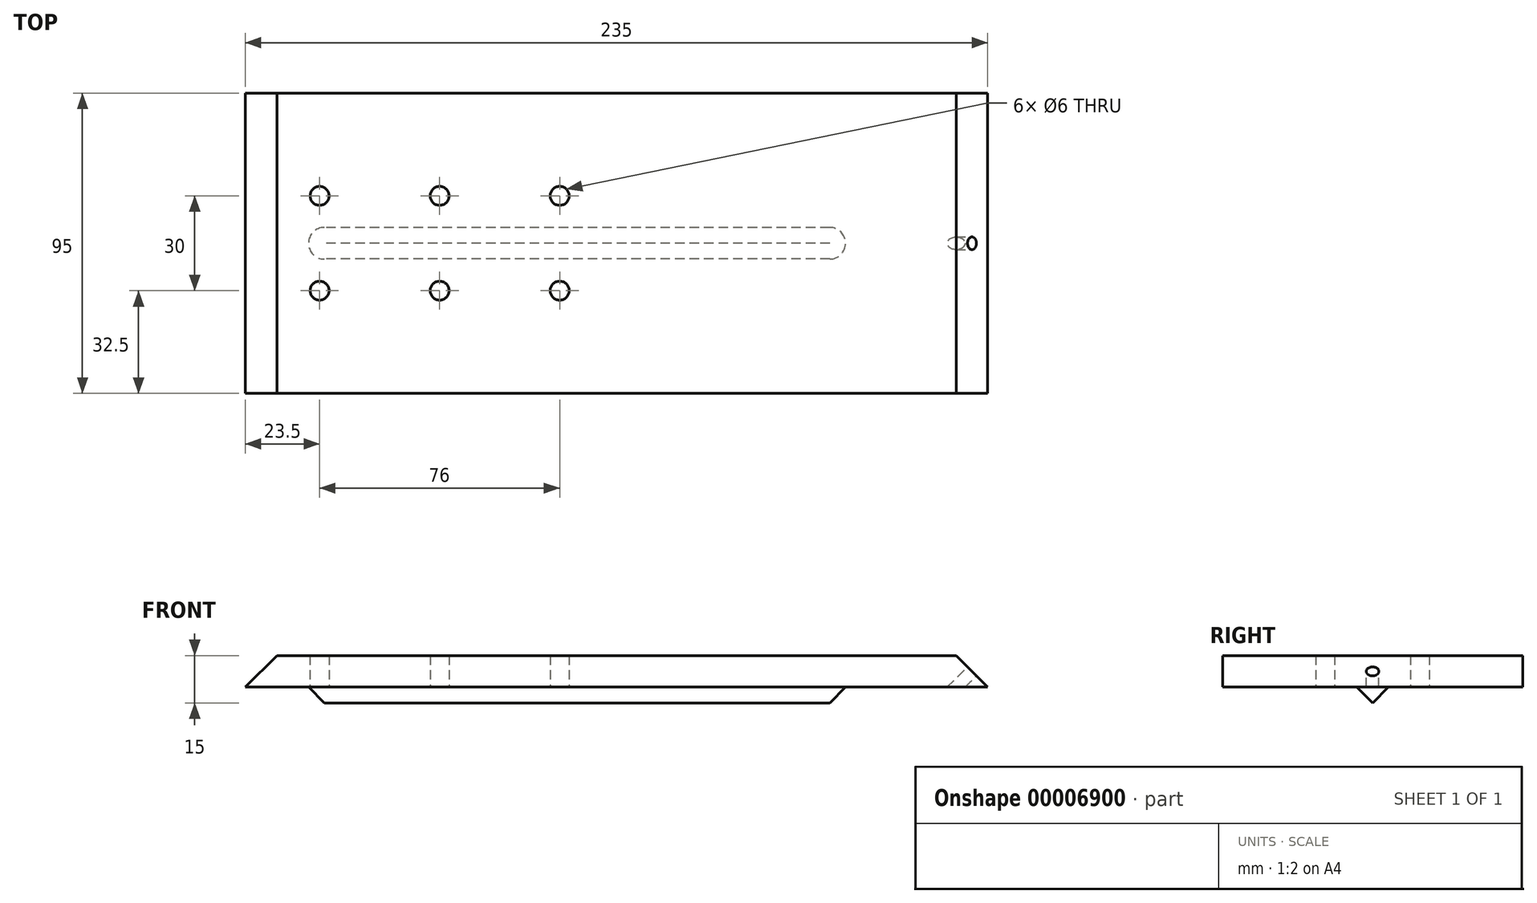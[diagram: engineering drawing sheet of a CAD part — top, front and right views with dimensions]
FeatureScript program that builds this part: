
annotation { "Feature Type Name" : "Feature", "Feature Type Description" : "" }
export const myFeature = defineFeature(function(context is Context, id is Id, definition is map)
    precondition{}
    {
        {
            var Q0;
            Q0=qCreatedBy(makeId("Top.planeOp"),FACE);
            var sketch = newSketch(context, id + "F0", { "sketchPlane" : qUnion([Q0])});
            skLineSegment(sketch, "E0.rect.bottom", {"start": v(125, -47.5) * mm, "end": v(-125, -47.5) * mm});
            skLineSegment(sketch, "E0.rect.top", {"start": v(125, 47.5) * mm, "end": v(-125, 47.5) * mm});
            skLineSegment(sketch, "E0.rect.left", {"start": v(125, -47.5) * mm, "end": v(125, 47.5) * mm});
            skLineSegment(sketch, "E0.rect.right", {"start": v(-125, -47.5) * mm, "end": v(-125, 47.5) * mm});
            skPoint(sketch, "E0.rect.middle", {"position": v(0, 0) * mm});
            skLineSegment(sketch, "E1", {"start": v(-125, 0) * mm, "end": v(125, 0) * mm, "construction": true});
            skLineSegment(sketch, "E2", {"start": v(-101.5, 47.5) * mm, "end": v(-101.5, -47.5) * mm, "construction": true});
            skLineSegment(sketch, "E3", {"start": v(-63.5, 47.5) * mm, "end": v(-63.5, -47.5) * mm, "construction": true});
            skLineSegment(sketch, "E4", {"start": v(-25.5, 47.5) * mm, "end": v(-25.5, -47.5) * mm, "construction": true});
            skCircle(sketch, "E5", {"center": v(-101.5, 15) * mm, "radius": 3 * mm});
            skCircle(sketch, "E6", {"center": v(-63.5, 15) * mm, "radius": 3 * mm});
            skCircle(sketch, "E7", {"center": v(-25.5, 15) * mm, "radius": 3 * mm});
            skCircle(sketch, "E8", {"center": v(-101.5, -15) * mm, "radius": 3 * mm});
            skCircle(sketch, "E9", {"center": v(-63.5, -15) * mm, "radius": 3 * mm});
            skCircle(sketch, "E10", {"center": v(-25.5, -15) * mm, "radius": 3 * mm});
            skSolve(sketch);
        }
        {
            var Q0;
            Q0=qSketchRegion(id+"F0",true);
            var Q1;
            Q1=makeQuery(id+"F0.imprint","IMPRINT",FACE,{"disambiguationData":[TD([[makeQuery(id+"F0.imprint","IMPRINT",EDGE,{"derivedFrom":sQuery(id+"F0.wireOp",EDGE,"E0.rect.bottom")}),-1.0]])]});
            extrude(context, id + "F1", {"entities" : qUnion([Q0, Q1]), "depth" : (15) * mm});
        }
        {
            var Q0;
            Q0=makeQuery(id+"F1.opExtrude","SWEPT_FACE",FACE,{"disambiguationData":[OSD([sQuery(id+"F0.wireOp",EDGE,"E0.rect.right")])]});
            var sketch = newSketch(context, id + "F2", { "sketchPlane" : qUnion([Q0])});
            skLineSegment(sketch, "E11", {"start": v(0, 0) * mm, "end": v(-5, 5) * mm});
            skLineSegment(sketch, "E12", {"start": v(0, 0) * mm, "end": v(5, 5) * mm});
            skLineSegment(sketch, "E13", {"start": v(-5, 5) * mm, "end": v(-47.5, 5) * mm});
            skLineSegment(sketch, "E14", {"start": v(5, 5) * mm, "end": v(47.5, 5) * mm});
            skSolve(sketch);
        }
        {
            var Q0;
            Q0 = qSketchRegion(id + "F2", true);
            var Q1;
            {var subQ2=sQuery(id+"F2.wireOp",EDGE,"E11");Q1=makeQuery(id+"F2.imprint","IMPRINT",FACE,{"disambiguationData":[TD([[makeQuery(id+"F2.imprint","IMPRINT",EDGE,{"derivedFrom":subQ2}),1.0]])]});}
            var Q2;
            {var subQ2=sQuery(id+"F2.wireOp",EDGE,"E12");Q2=makeQuery(id+"F2.imprint","IMPRINT",FACE,{"disambiguationData":[TD([[makeQuery(id+"F2.imprint","IMPRINT",EDGE,{"derivedFrom":subQ2}),-1.0]])]});}
            extrude(context, id + "F3", {"entities" : qUnion([Q0, Q1, Q2]), "operationType" : NewBodyOperationType.REMOVE, "endBound" : BoundingType.THROUGH_ALL, "oppositeDirection" : true, "depth" : 25 * mm});
        }
        {
            var Q0;
            Q0=makeQuery(id+"F1.opExtrude","SWEPT_FACE",FACE,{"disambiguationData":[OSD([sQuery(id+"F0.wireOp",EDGE,"E0.rect.right")])]});
            var sketch = newSketch(context, id + "F4", { "sketchPlane" : qUnion([Q0])});
            skLineSegment(sketch, "E15", {"start": v(-5, 5) * mm, "end": v(5, 5) * mm});
            skSolve(sketch);
        }
        {
            var Q0;
            Q0 = qSketchRegion(id + "F4", true);
            var Q1;
            Q1=makeQuery(id+"F4.imprint","IMPRINT",FACE,{"disambiguationData":[TD([[makeQuery(id+"F4.imprint","IMPRINT",EDGE,{"derivedFrom":sQuery(id+"F4.wireOp",EDGE,"E15")}),-1.0]])]});
            extrude(context, id + "F5", {"entities" : qUnion([Q0, Q1]), "operationType" : NewBodyOperationType.REMOVE, "oppositeDirection" : true, "depth" : 25 * mm});
        }
        {
            var Q0;
            Q0=makeQuery(id+"F5.boolean.opBoolean","COPY",FACE,{"derivedFrom":makeQuery(id+"F5.opExtrude","CAP_FACE",FACE,{"disambiguationData":[OSD([sQuery(id+"F2.wireOp",EDGE,"E11"),sQuery(id+"F2.wireOp",EDGE,"E12"),sQuery(id+"F4.wireOp",EDGE,"E15")])],"isStart":false})});
            var sketch = newSketch(context, id + "F6", { "sketchPlane" : qUnion([Q0])});
            skLineSegment(sketch, "E16", {"start": v(0, 0) * mm, "end": v(0, 5) * mm});
            skSolve(sketch);
        }
        {
            var Q0;
            {var subQ1=sQuery(id+"F6.wireOp",EDGE,"E16");Q0=makeQuery(id+"F6.imprint","IMPRINT",FACE,{"disambiguationData":[TD([[makeQuery(id+"F6.imprint","IMPRINT",EDGE,{"derivedFrom":subQ1}),1.0]])]});}
            var Q1;
            Q1=sQuery(id+"F6.wireOp",EDGE,"E16");
            revolve(context, id + "F7", {"operationType" : NewBodyOperationType.ADD, "entities" : qUnion([Q0]), "axis" : qUnion([Q1]), "revolveType" : RevolveType.FULL});
        }
        {
            var Q0;
            Q0=makeQuery(id+"F1.opExtrude","SWEPT_FACE",FACE,{"disambiguationData":[OSD([sQuery(id+"F0.wireOp",EDGE,"E0.rect.top")])]});
            var sketch = newSketch(context, id + "F8", { "sketchPlane" : qUnion([Q0])});
            skLineSegment(sketch, "E17", {"start": v(125, 5) * mm, "end": v(115, 15) * mm});
            skSolve(sketch);
        }
        {
            var Q0;
            Q0 = qSketchRegion(id + "F8", true);
            var Q1;
            {var subQ2=sQuery(id+"F8.wireOp",EDGE,"E17");Q1=makeQuery(id+"F8.imprint","IMPRINT",FACE,{"disambiguationData":[TD([[makeQuery(id+"F8.imprint","IMPRINT",EDGE,{"derivedFrom":subQ2}),-1.0]])]});}
            extrude(context, id + "F9", {"entities" : qUnion([Q0, Q1]), "operationType" : NewBodyOperationType.REMOVE, "endBound" : BoundingType.THROUGH_ALL, "oppositeDirection" : true, "depth" : 25 * mm});
        }
        {
            var Q0;
            Q0=makeQuery(id+"F1.opExtrude","SWEPT_FACE",FACE,{"disambiguationData":[OSD([sQuery(id+"F0.wireOp",EDGE,"E0.rect.left")])]});
            extrude(context, id + "F10", {"entities" : qUnion([Q0]), "operationType" : NewBodyOperationType.REMOVE, "oppositeDirection" : true, "depth" : (15) * mm});
        }
        {
            var Q0;
            Q0=makeQuery(id+"F10.boolean.opBoolean","COPY",FACE,{"derivedFrom":makeQuery(id+"F10.opExtrude","CAP_FACE",FACE,{"disambiguationData":[OSD([sQuery(id+"F0.wireOp",EDGE,"E0.rect.left")])],"isStart":false})});
            var sketch = newSketch(context, id + "F11", { "sketchPlane" : qUnion([Q0])});
            skLineSegment(sketch, "E18", {"start": v(-5, 5) * mm, "end": v(5, 5) * mm});
            skSolve(sketch);
        }
        {
            var Q0;
            Q0=makeQuery(id+"F11.imprint","IMPRINT",FACE,{"disambiguationData":[TD([[makeQuery(id+"F11.imprint","IMPRINT",EDGE,{"derivedFrom":sQuery(id+"F11.wireOp",EDGE,"E18")}),-1.0]])]});
            extrude(context, id + "F12", {"entities" : qUnion([Q0]), "operationType" : NewBodyOperationType.REMOVE, "oppositeDirection" : true, "depth" : (50) * mm});
        }
        {
            var Q0;
            Q0=makeQuery(id+"F12.boolean.opBoolean","COPY",FACE,{"derivedFrom":makeQuery(id+"F12.opExtrude","CAP_FACE",FACE,{"disambiguationData":[OSD([sQuery(id+"F0.wireOp",EDGE,"E0.rect.left"),sQuery(id+"F2.wireOp",EDGE,"E11"),sQuery(id+"F2.wireOp",EDGE,"E12"),sQuery(id+"F11.wireOp",EDGE,"E18")])],"isStart":false})});
            var sketch = newSketch(context, id + "F13", { "sketchPlane" : qUnion([Q0])});
            skLineSegment(sketch, "E19", {"start": v(0, 0) * mm, "end": v(0, 5) * mm});
            skSolve(sketch);
        }
        {
            var Q0;
            {var subQ1=sQuery(id+"F13.wireOp",EDGE,"E19");Q0=makeQuery(id+"F13.imprint","IMPRINT",FACE,{"disambiguationData":[TD([[makeQuery(id+"F13.imprint","IMPRINT",EDGE,{"derivedFrom":subQ1}),-1.0]])]});}
            var Q1;
            Q1=sQuery(id+"F13.wireOp",EDGE,"E19");
            revolve(context, id + "F14", {"operationType" : NewBodyOperationType.ADD, "entities" : qUnion([Q0]), "axis" : qUnion([Q1]), "revolveType" : RevolveType.FULL});
        }
        {
            var Q0;
            Q0=makeQuery(id+"F1.opExtrude","SWEPT_FACE",FACE,{"disambiguationData":[OSD([sQuery(id+"F0.wireOp",EDGE,"E0.rect.top")])]});
            var sketch = newSketch(context, id + "F15", { "sketchPlane" : qUnion([Q0])});
            skLineSegment(sketch, "E20", {"start": v(-110, 5) * mm, "end": v(-100, 15) * mm});
            skSolve(sketch);
        }
        {
            var Q0;
            Q0 = qSketchRegion(id + "F15", true);
            var Q1;
            {var subQ2=sQuery(id+"F15.wireOp",EDGE,"E20");Q1=makeQuery(id+"F15.imprint","IMPRINT",FACE,{"disambiguationData":[TD([[makeQuery(id+"F15.imprint","IMPRINT",EDGE,{"derivedFrom":subQ2}),1.0]])]});}
            extrude(context, id + "F16", {"entities" : qUnion([Q0, Q1]), "operationType" : NewBodyOperationType.REMOVE, "endBound" : BoundingType.THROUGH_ALL, "oppositeDirection" : true, "depth" : 25 * mm});
        }
        {
            var Q0;
            Q0=makeQuery(id+"F16.boolean.opBoolean","COPY",FACE,{"derivedFrom":makeQuery(id+"F16.opExtrude","SWEPT_FACE",FACE,{"disambiguationData":[OSD([sQuery(id+"F15.wireOp",EDGE,"E20")])]})});
            var sketch = newSketch(context, id + "F17", { "sketchPlane" : qUnion([Q0])});
            skLineSegment(sketch, "E21", {"start": v(0, -60.1) * mm, "end": v(0, -74.25) * mm, "construction": true});
            skCircle(sketch, "E22", {"center": v(0, -67.18) * mm, "radius": 2 * mm});
            skSolve(sketch);
        }
        {
            var Q0;
            Q0 = qSketchRegion(id + "F17", true);
            extrude(context, id + "F18", {"entities" : qUnion([Q0]), "operationType" : NewBodyOperationType.REMOVE, "endBound" : BoundingType.THROUGH_ALL, "oppositeDirection" : true, "depth" : 25 * mm});
        }
    });
